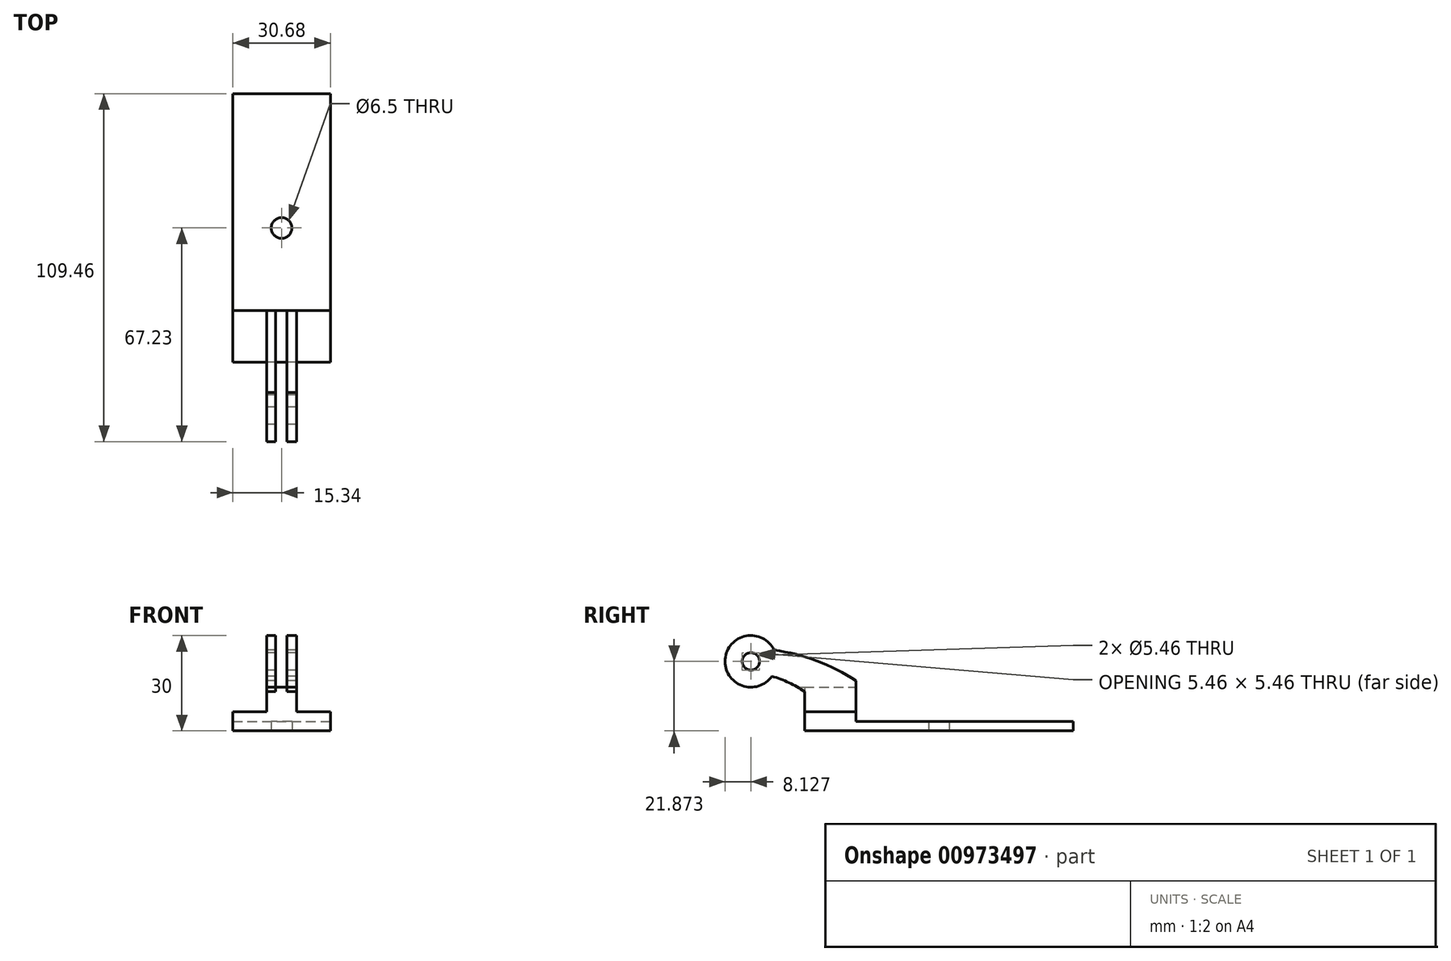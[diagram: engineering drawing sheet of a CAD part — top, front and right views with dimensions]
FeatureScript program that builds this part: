
annotation { "Feature Type Name" : "Feature", "Feature Type Description" : "" }
export const myFeature = defineFeature(function(context is Context, id is Id, definition is map)
    precondition{}
    {
        {
            var Q0;
            Q0=qCreatedBy(makeId("Top.planeOp"),FACE);
            var sketch = newSketch(context, id + "F0", { "sketchPlane" : qUnion([Q0])});
            skLineSegment(sketch, "E0.bottom", {"start": v(-15.34, 42.23) * mm, "end": v(15.34, 42.23) * mm});
            skLineSegment(sketch, "E0.top", {"start": v(-15.34, -42.23) * mm, "end": v(15.34, -42.23) * mm});
            skLineSegment(sketch, "E0.left", {"start": v(-15.34, 42.23) * mm, "end": v(-15.34, -42.23) * mm});
            skLineSegment(sketch, "E0.right", {"start": v(15.34, 42.23) * mm, "end": v(15.34, -42.23) * mm});
            skPoint(sketch, "E0.middle", {"position": v(0, 0) * mm});
            skCircle(sketch, "E1", {"center": v(0, 0) * mm, "radius": 3.25 * mm});
            skSolve(sketch);
        }
        {
            var Q0;
            Q0=makeQuery(id+"F0.imprint","IMPRINT",FACE,{"disambiguationData":[TD([[makeQuery(id+"F0.imprint","IMPRINT",EDGE,{"derivedFrom":sQuery(id+"F0.wireOp",EDGE,"E0.bottom")}),-1.0]])]});
            extrude(context, id + "F1", {"entities" : qUnion([Q0]), "depth" : 3 * mm, "offsetDistance" : 25 * mm});
        }
        {
            var Q0;
            Q0=makeQuery(id+"F1.opExtrude","CAP_FACE",FACE,{"disambiguationData":[OSD([sQuery(id+"F0.wireOp",EDGE,"E0.bottom"),sQuery(id+"F0.wireOp",EDGE,"E0.top"),sQuery(id+"F0.wireOp",EDGE,"E0.left"),sQuery(id+"F0.wireOp",EDGE,"E0.right"),sQuery(id+"F0.wireOp",EDGE,"E1")])],"isStart":false});
            var sketch = newSketch(context, id + "F2", { "sketchPlane" : qUnion([Q0])});
            skLineSegment(sketch, "E2.bottom", {"start": v(-15.34, -26.03) * mm, "end": v(15.34, -26.03) * mm});
            skLineSegment(sketch, "E2.top", {"start": v(-15.34, -42.23) * mm, "end": v(15.34, -42.23) * mm});
            skLineSegment(sketch, "E2.left", {"start": v(-15.34, -26.03) * mm, "end": v(-15.34, -42.23) * mm});
            skLineSegment(sketch, "E2.right", {"start": v(15.34, -26.03) * mm, "end": v(15.34, -42.23) * mm});
            skSolve(sketch);
        }
        {
            var Q0;
            Q0=qSketchRegion(id+"F2",true);
            extrude(context, id + "F3", {"entities" : qUnion([Q0]), "operationType" : NewBodyOperationType.ADD, "depth" : 3 * mm, "offsetDistance" : 25 * mm});
        }
        {
            var Q0;
            Q0=makeQuery(id+"F3.opExtrude","CAP_FACE",FACE,{"disambiguationData":[OSD([sQuery(id+"F2.wireOp",EDGE,"E2.bottom"),sQuery(id+"F2.wireOp",EDGE,"E2.top"),sQuery(id+"F2.wireOp",EDGE,"E2.left"),sQuery(id+"F2.wireOp",EDGE,"E2.right")])],"isStart":false});
            var sketch = newSketch(context, id + "F4", { "sketchPlane" : qUnion([Q0])});
            skLineSegment(sketch, "E3.bottom", {"start": v(4.75, -42.23) * mm, "end": v(-4.75, -42.23) * mm});
            skLineSegment(sketch, "E3.top", {"start": v(4.75, 42.23) * mm, "end": v(-4.75, 42.23) * mm});
            skLineSegment(sketch, "E3.left", {"start": v(4.75, -42.23) * mm, "end": v(4.75, 42.23) * mm});
            skLineSegment(sketch, "E3.right", {"start": v(-4.75, -42.23) * mm, "end": v(-4.75, 42.23) * mm});
            skPoint(sketch, "E3.middle", {"position": v(0, 0) * mm});
            skLineSegment(sketch, "E4", {"start": v(-4.75, -26.03) * mm, "end": v(4.75, -26.03) * mm});
            skLineSegment(sketch, "E5", {"start": v(4.75, -26.03) * mm, "end": v(4.75, -42.23) * mm});
            skLineSegment(sketch, "E6", {"start": v(-4.75, -42.23) * mm, "end": v(-4.75, -26.03) * mm});
            skSolve(sketch);
        }
        {
            var Q0;
            {var subQ0=sQuery(id+"F4.wireOp",EDGE,"E3.bottom");Q0=makeQuery(id+"F4.imprint","IMPRINT",FACE,{"disambiguationData":[TD([[makeQuery(id+"F4.imprint","IMPRINT",EDGE,{"derivedFrom":subQ0}),1.0]])]});}
            extrude(context, id + "F5", {"entities" : qUnion([Q0]), "operationType" : NewBodyOperationType.ADD, "depth" : 24 * mm, "offsetDistance" : 25 * mm});
        }
        {
            var Q0;
            Q0=makeQuery(id+"F5.boolean.opBoolean","MERGE",FACE,{"derivedFrom":[makeQuery(id+"F3.opExtrude","SWEPT_FACE",FACE,{"disambiguationData":[OSD([sQuery(id+"F2.wireOp",EDGE,"E2.bottom")])]}),makeQuery(id+"F5.opExtrude","SWEPT_FACE",FACE,{"disambiguationData":[OSD([sQuery(id+"F4.wireOp",EDGE,"E4")])]})]});
            var sketch = newSketch(context, id + "F6", { "sketchPlane" : qUnion([Q0])});
            skLineSegment(sketch, "E7.bottom", {"start": v(-1.65, 30) * mm, "end": v(1.85, 30) * mm});
            skLineSegment(sketch, "E7.top", {"start": v(-1.65, 13.75) * mm, "end": v(1.85, 13.75) * mm});
            skLineSegment(sketch, "E7.left", {"start": v(-1.65, 30) * mm, "end": v(-1.65, 13.75) * mm});
            skLineSegment(sketch, "E7.right", {"start": v(1.85, 30) * mm, "end": v(1.85, 13.75) * mm});
            skSolve(sketch);
        }
        {
            var Q0;
            Q0=makeQuery(id+"F6.imprint","IMPRINT",FACE,{"disambiguationData":[TD([[makeQuery(id+"F6.imprint","IMPRINT",EDGE,{"derivedFrom":sQuery(id+"F6.wireOp",EDGE,"E7.bottom")}),1.0]])]});
            extrude(context, id + "F7", {"entities" : qUnion([Q0]), "operationType" : NewBodyOperationType.REMOVE, "oppositeDirection" : true, "depth" : 18 * mm, "offsetDistance" : 25 * mm});
        }
        {
            var Q0;
            Q0=makeQuery(id+"F5.boolean.opBoolean","MERGE",FACE,{"derivedFrom":[makeQuery(id+"F3.boolean.opBoolean","MERGE",FACE,{"derivedFrom":[makeQuery(id+"F1.opExtrude","SWEPT_FACE",FACE,{"disambiguationData":[OSD([sQuery(id+"F0.wireOp",EDGE,"E0.top")])]}),makeQuery(id+"F3.opExtrude","SWEPT_FACE",FACE,{"disambiguationData":[OSD([sQuery(id+"F2.wireOp",EDGE,"E2.top")])]})]}),makeQuery(id+"F5.opExtrude","SWEPT_FACE",FACE,{"disambiguationData":[OSD([sQuery(id+"F4.wireOp",EDGE,"E3.bottom")])]})]});
            var sketch = newSketch(context, id + "F8", { "sketchPlane" : qUnion([Q0])});
            skLineSegment(sketch, "E8.left", {"start": v(-4.75, 30) * mm, "end": v(-4.75, 12.36) * mm});
            skLineSegment(sketch, "E9.bottom", {"start": v(4.75, 30) * mm, "end": v(-4.75, 30) * mm});
            skLineSegment(sketch, "E9.top", {"start": v(4.75, 12.36) * mm, "end": v(-4.75, 12.36) * mm});
            skLineSegment(sketch, "E9.left", {"start": v(4.75, 30) * mm, "end": v(4.75, 12.36) * mm});
            skLineSegment(sketch, "E10.bottom", {"start": v(-1.85, 13.75) * mm, "end": v(1.65, 13.75) * mm});
            skLineSegment(sketch, "E10.top", {"start": v(-1.85, 12.36) * mm, "end": v(1.65, 12.36) * mm});
            skLineSegment(sketch, "E10.left", {"start": v(-1.85, 13.75) * mm, "end": v(-1.85, 12.36) * mm});
            skLineSegment(sketch, "E10.right", {"start": v(1.65, 13.75) * mm, "end": v(1.65, 12.36) * mm});
            skSolve(sketch);
        }
        {
            var Q0;
            {var subQ1=sQuery(id+"F8.wireOp",EDGE,"E8.left");Q0=makeQuery(id+"F8.imprint","IMPRINT",FACE,{"disambiguationData":[TD([[makeQuery(id+"F8.imprint","IMPRINT",EDGE,{"derivedFrom":subQ1}),1.0]])]});}
            var Q1;
            {var subQ5=sQuery(id+"F8.wireOp",EDGE,"E9.left");Q1=makeQuery(id+"F8.imprint","IMPRINT",FACE,{"disambiguationData":[TD([[makeQuery(id+"F8.imprint","IMPRINT",EDGE,{"derivedFrom":subQ5}),-1.0]])]});}
            extrude(context, id + "F9", {"entities" : qUnion([Q0, Q1]), "operationType" : NewBodyOperationType.ADD, "depth" : 25 * mm, "offsetDistance" : 25 * mm});
        }
        {
            var Q0;
            Q0=makeQuery(id+"F9.boolean.opBoolean","MERGE",FACE,{"derivedFrom":[makeQuery(id+"F5.opExtrude","SWEPT_FACE",FACE,{"disambiguationData":[OSD([sQuery(id+"F4.wireOp",EDGE,"E3.right")])]}),makeQuery(id+"F9.opExtrude","SWEPT_FACE",FACE,{"disambiguationData":[OSD([sQuery(id+"F8.wireOp",EDGE,"E8.left")])]})]});
            var sketch = newSketch(context, id + "F10", { "sketchPlane" : qUnion([Q0])});
            skLineSegment(sketch, "E11", {"start": v(42.23, 30) * mm, "end": v(46.63, 30) * mm});
            skLineSegment(sketch, "E12", {"start": v(26.03, 30) * mm, "end": v(26.03, 28.45) * mm});
            skPoint(sketch, "E13", {"position": v(42.23, 19.59) * mm});
            skCircle(sketch, "E14", {"center": v(-59, 21.82) * mm, "radius": 8.13 * mm});
            skCircle(sketch, "E15", {"center": v(-59, 21.82) * mm, "radius": 2.73 * mm});
            skPoint(sketch, "E16.center.orphan", {"position": v(51.63, 19.59) * mm});
            skCircle(sketch, "E17", {"center": v(59.1, 21.87) * mm, "radius": 8.13 * mm});
            skCircle(sketch, "E18", {"center": v(59.1, 21.87) * mm, "radius": 2.73 * mm});
            skArc(sketch, "E19", {"start": v(52.48, 17.17) * mm, "mid": v(47.16, 15.17) * mm, "end": v(42.23, 12.36) * mm});
            skArc(sketch, "E20", {"start": v(51.8, 25.43) * mm, "mid": v(38.38, 22.06) * mm, "end": v(26.03, 15.8) * mm});
            skSolve(sketch);
        }
        {
            var Q0;
            {var subQ0=sQuery(id+"F10.wireOp",EDGE,"E17");var subQ1=sQuery(id+"F8.wireOp",EDGE,"E8.left");var subQ4=makeQuery(id+"F9.opExtrude","CAP_EDGE",EDGE,{"disambiguationData":[OSD([subQ1])],"isStart":false});var subQ5=makeQuery(id+"F10.imprint","INTERSECT",VERTEX,{"derivedFrom":[subQ4,subQ0]});Q0=makeQuery(id+"F10.imprint","IMPRINT",FACE,{"disambiguationData":[TD([[makeQuery(id+"F10.imprint","IMPRINT",EDGE,{"disambiguationData":[TD([[subQ5,-1.0]])],"derivedFrom":subQ0}),-1.0]])]});}
            var Q1;
            {var subQ0=sQuery(id+"F10.wireOp",EDGE,"E19");Q1=makeQuery(id+"F10.imprint","IMPRINT",FACE,{"disambiguationData":[TD([[makeQuery(id+"F10.imprint","IMPRINT",EDGE,{"derivedFrom":subQ0}),1.0]])]});}
            var Q2;
            Q2=makeQuery(id+"F10.imprint","IMPRINT",FACE,{"disambiguationData":[TD([[makeQuery(id+"F10.imprint","IMPRINT",EDGE,{"derivedFrom":sQuery(id+"F10.wireOp",EDGE,"E18")}),1.0]])]});
            var Q3;
            {var subQ0=sQuery(id+"F10.wireOp",EDGE,"E12");Q3=makeQuery(id+"F10.imprint","IMPRINT",FACE,{"disambiguationData":[TD([[makeQuery(id+"F10.imprint","IMPRINT",EDGE,{"derivedFrom":subQ0}),1.0]])]});}
            extrude(context, id + "F11", {"entities" : qUnion([Q0, Q1, Q2, Q3]), "operationType" : NewBodyOperationType.REMOVE, "endBound" : BoundingType.THROUGH_ALL, "oppositeDirection" : true, "depth" : 25 * mm, "offsetDistance" : 25 * mm});
        }
    });
